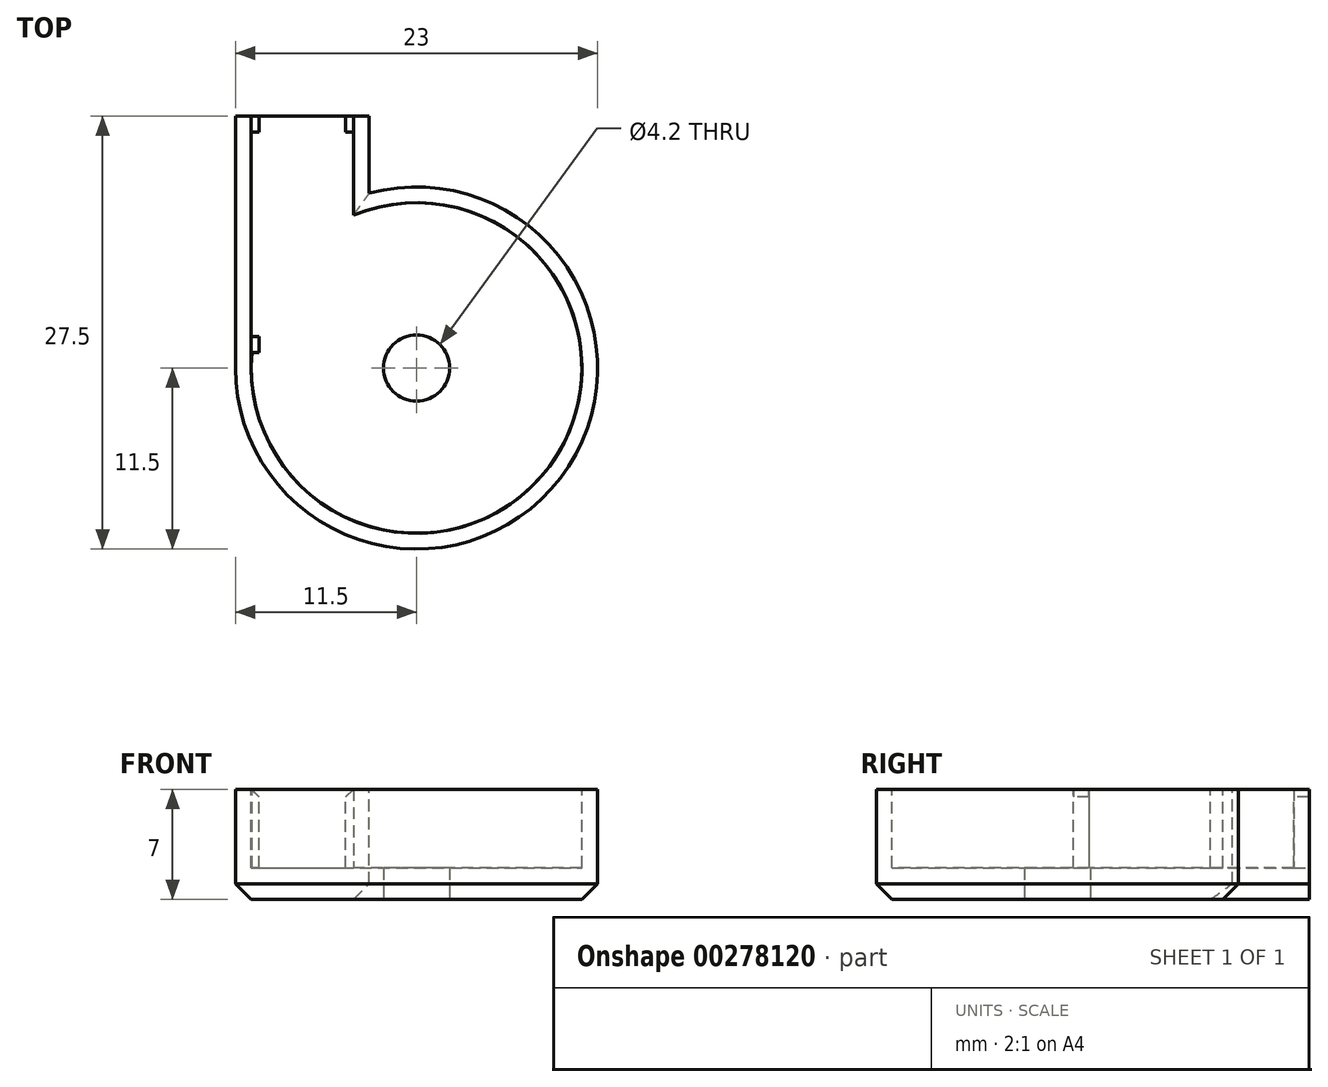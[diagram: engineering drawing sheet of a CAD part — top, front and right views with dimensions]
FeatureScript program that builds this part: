
annotation { "Feature Type Name" : "Feature", "Feature Type Description" : "" }
export const myFeature = defineFeature(function(context is Context, id is Id, definition is map)
    precondition{}
    {
        {
            var Q0;
            Q0=qCreatedBy(makeId("Top.planeOp"),FACE);
            var sketch = newSketch(context, id + "F0", { "sketchPlane" : qUnion([Q0])});
            skCircle(sketch, "E0", {"center": v(0, 0) * mm, "radius": 11.5 * mm});
            skCircle(sketch, "E1", {"center": v(0, 0) * mm, "radius": 2.1 * mm});
            skSolve(sketch);
        }
        {
            var Q0;
            Q0=qSketchRegion(id+"F0",true);
            extrude(context, id + "F1", {"entities" : qUnion([Q0]), "depth" : 7 * mm});
        }
        {
            var Q0;
            Q0=makeQuery(id+"F1.opExtrude","CAP_FACE",FACE,{"disambiguationData":[OSD([sQuery(id+"F0.wireOp",EDGE,"E0")])],"isStart":false});
            var sketch = newSketch(context, id + "F2", { "sketchPlane" : qUnion([Q0])});
            skCircle(sketch, "E2", {"center": v(0, 0) * mm, "radius": 10.5 * mm});
            skSolve(sketch);
        }
        {
            var Q0;
            Q0=qSketchRegion(id+"F2",true);
            extrude(context, id + "F3", {"entities" : qUnion([Q0]), "operationType" : NewBodyOperationType.REMOVE, "oppositeDirection" : true, "depth" : 5 * mm});
        }
        {
            var Q0;
            Q0=makeQuery(id+"F1.opExtrude","CAP_FACE",FACE,{"disambiguationData":[OSD([sQuery(id+"F0.wireOp",EDGE,"E0"),sQuery(id+"F0.wireOp",EDGE,"E1")])],"isStart":false});
            var sketch = newSketch(context, id + "F4", { "sketchPlane" : qUnion([Q0])});
            skLineSegment(sketch, "E3", {"start": v(-11.5, 0) * mm, "end": v(-11.5, 16) * mm});
            skLineSegment(sketch, "E4", {"start": v(-11.5, 16) * mm, "end": v(-3, 16) * mm});
            skLineSegment(sketch, "E5", {"start": v(-3, 16) * mm, "end": v(-3, 11.1) * mm});
            skLineSegment(sketch, "E6", {"start": v(-10.5, 0) * mm, "end": v(-10.5, 16) * mm});
            skLineSegment(sketch, "E7", {"start": v(-3, 16) * mm, "end": v(-4, 16) * mm});
            skLineSegment(sketch, "E8", {"start": v(-4, 16) * mm, "end": v(-4, 10.78) * mm});
            skSolve(sketch);
        }
        {
            var Q0;
            {var subQ0=sQuery(id+"F4.wireOp",EDGE,"E3");Q0=makeQuery(id+"F4.imprint","IMPRINT",FACE,{"disambiguationData":[TD([[makeQuery(id+"F4.imprint","IMPRINT",EDGE,{"derivedFrom":subQ0}),-1.0]])]});}
            var Q1;
            {var subQ0=sQuery(id+"F4.wireOp",EDGE,"E5");Q1=makeQuery(id+"F4.imprint","IMPRINT",FACE,{"disambiguationData":[TD([[makeQuery(id+"F4.imprint","IMPRINT",EDGE,{"derivedFrom":subQ0}),-1.0]])]});}
            extrude(context, id + "F5", {"entities" : qUnion([Q0, Q1]), "operationType" : NewBodyOperationType.ADD, "oppositeDirection" : true, "depth" : 7 * mm});
        }
        {
            var Q0;
            Q0=makeQuery(id+"F5.opExtrude","SWEPT_FACE",FACE,{"disambiguationData":[OSD([sQuery(id+"F4.wireOp",EDGE,"E4")])]});
            var sketch = newSketch(context, id + "F6", { "sketchPlane" : qUnion([Q0])});
            skLineSegment(sketch, "E9.bottom", {"start": v(11.5, 0) * mm, "end": v(3, 0) * mm});
            skLineSegment(sketch, "E9.top", {"start": v(11.5, 2) * mm, "end": v(3, 2) * mm});
            skLineSegment(sketch, "E9.left", {"start": v(11.5, 0) * mm, "end": v(11.5, 2) * mm});
            skLineSegment(sketch, "E9.right", {"start": v(3, 0) * mm, "end": v(3, 2) * mm});
            skSolve(sketch);
        }
        {
            var Q0;
            Q0=qSketchRegion(id+"F6",true);
            extrude(context, id + "F7", {"entities" : qUnion([Q0]), "operationType" : NewBodyOperationType.ADD, "oppositeDirection" : true, "depth" : 12.8 * mm});
        }
        {
            var Q0;
            Q0=makeQuery(id+"F7.boolean.opBoolean","MERGE",FACE,{"derivedFrom":[makeQuery(id+"F5.opExtrude","SWEPT_FACE",FACE,{"disambiguationData":[OSD([sQuery(id+"F4.wireOp",EDGE,"E4")])]}),makeQuery(id+"F5.opExtrude","SWEPT_FACE",FACE,{"disambiguationData":[OSD([sQuery(id+"F4.wireOp",EDGE,"E7")])]}),makeQuery(id+"F7.opExtrude","CAP_FACE",FACE,{"disambiguationData":[OSD([sQuery(id+"F6.wireOp",EDGE,"E9.bottom"),sQuery(id+"F6.wireOp",EDGE,"E9.top"),sQuery(id+"F6.wireOp",EDGE,"E9.left"),sQuery(id+"F6.wireOp",EDGE,"E9.right")])],"isStart":true})]});
            var sketch = newSketch(context, id + "F8", { "sketchPlane" : qUnion([Q0])});
            skLineSegment(sketch, "E10.bottom", {"start": v(10.5, 7) * mm, "end": v(4, 7) * mm});
            skLineSegment(sketch, "E10.top", {"start": v(10.5, 2) * mm, "end": v(4, 2) * mm});
            skLineSegment(sketch, "E10.left", {"start": v(10.5, 7) * mm, "end": v(10.5, 2) * mm});
            skLineSegment(sketch, "E10.right", {"start": v(4, 7) * mm, "end": v(4, 2) * mm});
            skSolve(sketch);
        }
        {
            var Q0;
            Q0=makeQuery(id+"F8.imprint","IMPRINT",FACE,{"disambiguationData":[TD([[makeQuery(id+"F8.imprint","IMPRINT",EDGE,{"derivedFrom":sQuery(id+"F8.wireOp",EDGE,"E10.bottom")}),1.0]])]});
            extrude(context, id + "F9", {"entities" : qUnion([Q0]), "operationType" : NewBodyOperationType.REMOVE, "oppositeDirection" : true, "depth" : 15 * mm});
        }
        {
            var Q0;
            Q0=makeQuery(id+"F9.boolean.opBoolean","MERGE",FACE,{"derivedFrom":[makeQuery(id+"F5.opExtrude","SWEPT_FACE",FACE,{"disambiguationData":[OSD([sQuery(id+"F4.wireOp",EDGE,"E6")])]}),makeQuery(id+"F9.opExtrude","SWEPT_FACE",FACE,{"disambiguationData":[OSD([sQuery(id+"F8.wireOp",EDGE,"E10.left")])]})]});
            var sketch = newSketch(context, id + "F10", { "sketchPlane" : qUnion([Q0])});
            skLineSegment(sketch, "E11.bottom", {"start": v(1, 7) * mm, "end": v(2, 7) * mm});
            skLineSegment(sketch, "E11.top", {"start": v(1, 2) * mm, "end": v(2, 2) * mm});
            skLineSegment(sketch, "E11.left", {"start": v(1, 7) * mm, "end": v(1, 2) * mm});
            skLineSegment(sketch, "E11.right", {"start": v(2, 7) * mm, "end": v(2, 2) * mm});
            skLineSegment(sketch, "E12.bottom", {"start": v(16, 2) * mm, "end": v(15, 2) * mm});
            skLineSegment(sketch, "E12.top", {"start": v(16, 7) * mm, "end": v(15, 7) * mm});
            skLineSegment(sketch, "E12.left", {"start": v(16, 2) * mm, "end": v(16, 7) * mm});
            skLineSegment(sketch, "E12.right", {"start": v(15, 2) * mm, "end": v(15, 7) * mm});
            skSolve(sketch);
        }
        {
            var Q0;
            Q0=qSketchRegion(id+"F10",true);
            extrude(context, id + "F11", {"entities" : qUnion([Q0]), "operationType" : NewBodyOperationType.ADD, "depth" : .5 * mm});
        }
        {
            var Q0;
            Q0=makeQuery(id+"F9.boolean.opBoolean","MERGE",FACE,{"derivedFrom":[makeQuery(id+"F5.opExtrude","SWEPT_FACE",FACE,{"disambiguationData":[OSD([sQuery(id+"F4.wireOp",EDGE,"E8")])]}),makeQuery(id+"F9.opExtrude","SWEPT_FACE",FACE,{"disambiguationData":[OSD([sQuery(id+"F8.wireOp",EDGE,"E10.right")])]})]});
            var sketch = newSketch(context, id + "F12", { "sketchPlane" : qUnion([Q0])});
            skLineSegment(sketch, "E13.bottom", {"start": v(-16, 7) * mm, "end": v(-15, 7) * mm});
            skLineSegment(sketch, "E13.top", {"start": v(-16, 2) * mm, "end": v(-15, 2) * mm});
            skLineSegment(sketch, "E13.left", {"start": v(-16, 7) * mm, "end": v(-16, 2) * mm});
            skLineSegment(sketch, "E13.right", {"start": v(-15, 7) * mm, "end": v(-15, 2) * mm});
            skSolve(sketch);
        }
        {
            var Q0;
            Q0=qSketchRegion(id+"F12",true);
            extrude(context, id + "F13", {"entities" : qUnion([Q0]), "operationType" : NewBodyOperationType.ADD, "depth" : .5 * mm});
        }
        {
            var Q0;
            Q0=makeQuery(id+"F11.opExtrude","CAP_EDGE",EDGE,{"disambiguationData":[OSD([sQuery(id+"F10.wireOp",EDGE,"E11.bottom")])],"isStart":false});
            var Q1;
            Q1=makeQuery(id+"F11.opExtrude","CAP_EDGE",EDGE,{"disambiguationData":[OSD([sQuery(id+"F10.wireOp",EDGE,"E12.top")])],"isStart":false});
            var Q2;
            Q2=makeQuery(id+"F13.opExtrude","CAP_EDGE",EDGE,{"disambiguationData":[OSD([sQuery(id+"F12.wireOp",EDGE,"E13.bottom")])],"isStart":false});
            chamfer(context, id + "F14", {"entities" : qUnion([Q0, Q1, Q2]), "width" : .5 * mm, "tangentPropagation" : true});
        }
        {
            var Q0;
            {var subQ0=sQuery(id+"F4.wireOp",EDGE,"E3");var subQ1=sQuery(id+"F0.wireOp",EDGE,"E0");Q0=makeQuery(id+"F5.boolean.opBoolean","SPLIT",EDGE,{"disambiguationData":[TD([makeQuery(id+"F5.opExtrude","SWEPT_FACE",FACE,{"disambiguationData":[OSD([subQ0])]})])],"derivedFrom":makeQuery(id+"F1.opExtrude","CAP_EDGE",EDGE,{"disambiguationData":[OSD([subQ1])],"isStart":true})});}
            var Q1;
            Q1=makeQuery(id+"F5.opExtrude","CAP_EDGE",EDGE,{"disambiguationData":[OSD([sQuery(id+"F4.wireOp",EDGE,"E5")])],"isStart":false});
            var Q2;
            Q2=makeQuery(id+"F5.opExtrude","CAP_EDGE",EDGE,{"disambiguationData":[OSD([sQuery(id+"F4.wireOp",EDGE,"E3")])],"isStart":false});
            chamfer(context, id + "F15", {"entities" : qUnion([Q0, Q1, Q2]), "width" : 1 * mm, "tangentPropagation" : true});
        }
    });
